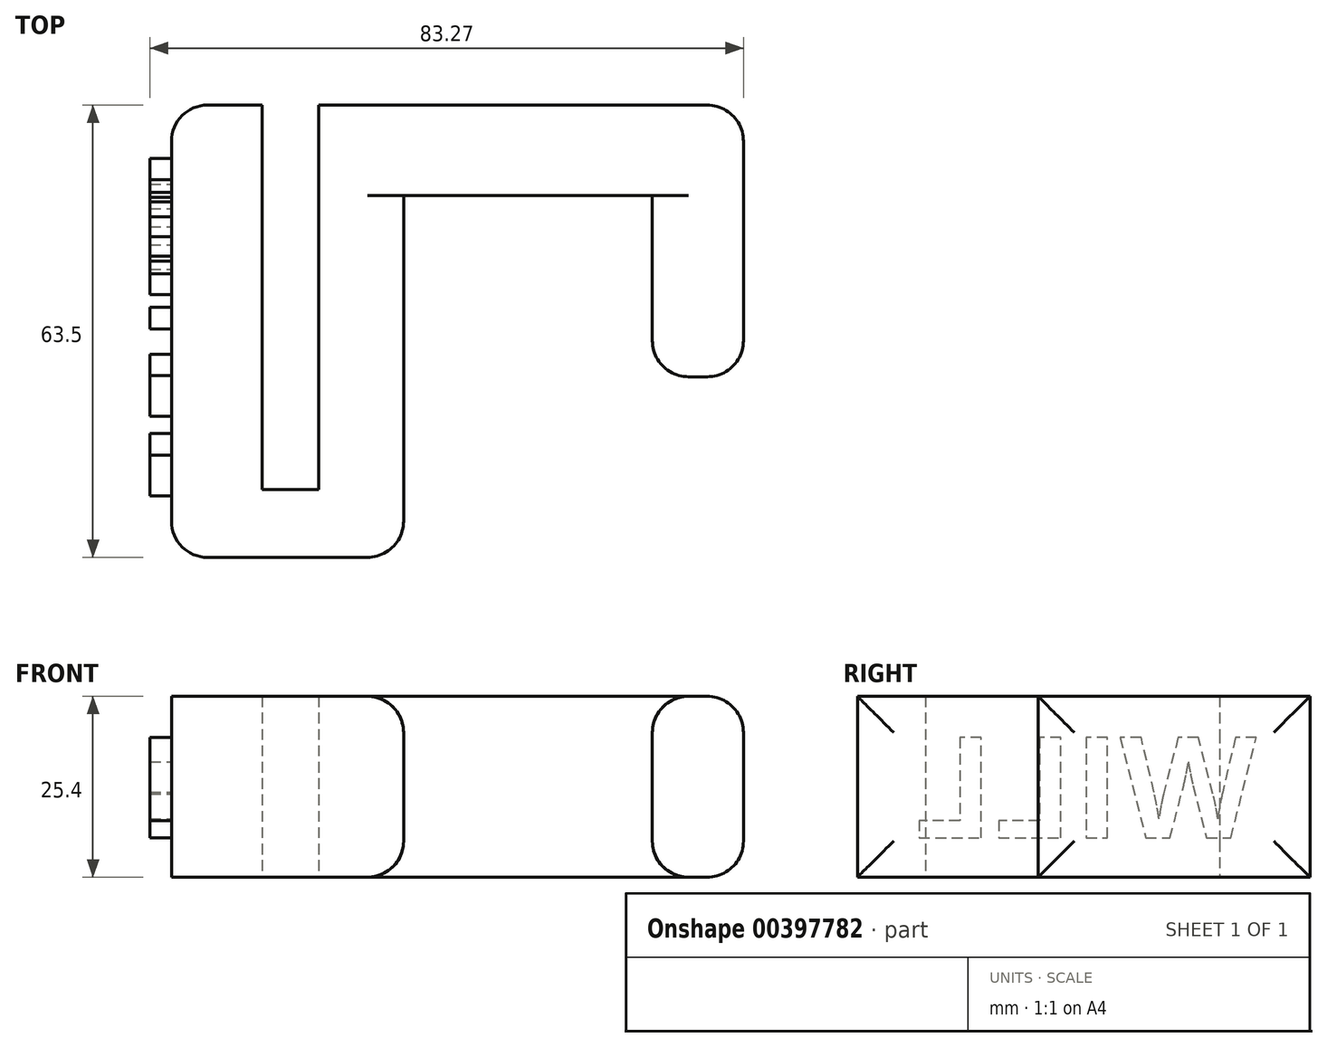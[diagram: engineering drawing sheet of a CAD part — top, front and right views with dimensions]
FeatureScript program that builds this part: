
annotation { "Feature Type Name" : "Feature", "Feature Type Description" : "" }
export const myFeature = defineFeature(function(context is Context, id is Id, definition is map)
    precondition{}
    {
        {
            var Q0;
            Q0=qCreatedBy(makeId("Top.planeOp"),FACE);
            var sketch = newSketch(context, id + "F0", { "sketchPlane" : qUnion([Q0])});
            skLineSegment(sketch, "E0", {"start": v(0, 0) * mm, "end": v(0, 63.5) * mm});
            skLineSegment(sketch, "E1", {"start": v(0, 63.5) * mm, "end": v(12.7, 63.5) * mm});
            skLineSegment(sketch, "E2", {"start": v(12.7, 63.5) * mm, "end": v(12.7, 9.53) * mm});
            skLineSegment(sketch, "E3", {"start": v(12.7, 9.53) * mm, "end": v(20.64, 9.53) * mm});
            skLineSegment(sketch, "E4", {"start": v(20.64, 9.53) * mm, "end": v(20.64, 63.5) * mm});
            skLineSegment(sketch, "E5", {"start": v(20.64, 63.5) * mm, "end": v(80.27, 63.5) * mm});
            skLineSegment(sketch, "E6", {"start": v(80.27, 63.5) * mm, "end": v(80.27, 25.35) * mm});
            skLineSegment(sketch, "E7", {"start": v(80.27, 25.35) * mm, "end": v(67.48, 25.35) * mm});
            skLineSegment(sketch, "E8", {"start": v(67.48, 25.35) * mm, "end": v(67.48, 50.8) * mm});
            skLineSegment(sketch, "E9", {"start": v(67.48, 50.8) * mm, "end": v(32.58, 50.8) * mm});
            skLineSegment(sketch, "E10", {"start": v(32.58, 50.8) * mm, "end": v(32.58, 0) * mm});
            skLineSegment(sketch, "E11", {"start": v(32.58, 0) * mm, "end": v(0, 0) * mm});
            skSolve(sketch);
        }
        {
            var Q0;
            Q0=makeQuery(id+"F0.imprint","IMPRINT",FACE,{"disambiguationData":[TD([[makeQuery(id+"F0.imprint","IMPRINT",EDGE,{"derivedFrom":sQuery(id+"F0.wireOp",EDGE,"E0")}),-1.0]])]});
            extrude(context, id + "F1", {"entities" : qUnion([Q0]), "depth" : 25.4 * mm});
        }
        {
            var Q0;
            Q0=makeQuery(id+"F1.opExtrude","SWEPT_EDGE",EDGE,{"disambiguationData":[OSD([sQuery(id+"F0.wireOp",EDGE,"E5"),sQuery(id+"F0.wireOp",EDGE,"E6")])]});
            var Q1;
            Q1=makeQuery(id+"F1.opExtrude","SWEPT_EDGE",EDGE,{"disambiguationData":[OSD([sQuery(id+"F0.wireOp",EDGE,"E6"),sQuery(id+"F0.wireOp",EDGE,"E7")])]});
            var Q2;
            Q2=makeQuery(id+"F1.opExtrude","SWEPT_EDGE",EDGE,{"disambiguationData":[OSD([sQuery(id+"F0.wireOp",EDGE,"E7"),sQuery(id+"F0.wireOp",EDGE,"E8")])]});
            var Q3;
            Q3=makeQuery(id+"F1.opExtrude","SWEPT_EDGE",EDGE,{"disambiguationData":[OSD([sQuery(id+"F0.wireOp",EDGE,"E10"),sQuery(id+"F0.wireOp",EDGE,"E11")])]});
            var Q4;
            Q4=makeQuery(id+"F1.opExtrude","SWEPT_EDGE",EDGE,{"disambiguationData":[OSD([sQuery(id+"F0.wireOp",EDGE,"E0"),sQuery(id+"F0.wireOp",EDGE,"E11")])]});
            var Q5;
            Q5=makeQuery(id+"F1.opExtrude","SWEPT_EDGE",EDGE,{"disambiguationData":[OSD([sQuery(id+"F0.wireOp",EDGE,"E0"),sQuery(id+"F0.wireOp",EDGE,"E1")])]});
            var Q6;
            Q6=makeQuery(id+"F1.opExtrude","CAP_EDGE",EDGE,{"disambiguationData":[OSD([sQuery(id+"F0.wireOp",EDGE,"E10")])],"isStart":false});
            var Q7;
            Q7=makeQuery(id+"F1.opExtrude","CAP_EDGE",EDGE,{"disambiguationData":[OSD([sQuery(id+"F0.wireOp",EDGE,"E8")])],"isStart":false});
            var Q8;
            Q8=makeQuery(id+"F1.opExtrude","CAP_EDGE",EDGE,{"disambiguationData":[OSD([sQuery(id+"F0.wireOp",EDGE,"E6")])],"isStart":false});
            var Q9;
            Q9=makeQuery(id+"F1.opExtrude","CAP_EDGE",EDGE,{"disambiguationData":[OSD([sQuery(id+"F0.wireOp",EDGE,"E6")])],"isStart":true});
            var Q10;
            Q10=makeQuery(id+"F1.opExtrude","CAP_EDGE",EDGE,{"disambiguationData":[OSD([sQuery(id+"F0.wireOp",EDGE,"E8")])],"isStart":true});
            var Q11;
            Q11=makeQuery(id+"F1.opExtrude","CAP_EDGE",EDGE,{"disambiguationData":[OSD([sQuery(id+"F0.wireOp",EDGE,"E10")])],"isStart":true});
            fillet(context, id + "F2", {"entities" : qUnion([Q0, Q1, Q2, Q3, Q4, Q5, Q6, Q7, Q8, Q9, Q10, Q11]), "radius" : 5.08 * mm, "tangentPropagation" : true, "allowEdgeOverflow" : false});
        }
        {
            var Q0;
            Q0=makeQuery(id+"F1.opExtrude","SWEPT_FACE",FACE,{"disambiguationData":[OSD([sQuery(id+"F0.wireOp",EDGE,"E0")])]});
            var sketch = newSketch(context, id + "F3", { "sketchPlane" : qUnion([Q0])});
            skText(sketch, "E12", { "text": "WILL", "fontName": "OpenSans-Bold.ttf"});
            const initialGuessF3  = {"E12": [-0.05599, 0.0055, 1, 0, 0.01424]};
            skSetInitialGuess(sketch, initialGuessF3);
            skSolve(sketch);
        }
        {
            var Q0;
            Q0=qSketchRegion(id+"F3",true);
            extrude(context, id + "F4", {"entities" : qUnion([Q0]), "operationType" : NewBodyOperationType.ADD, "depth" : 3 * mm});
        }
    });
